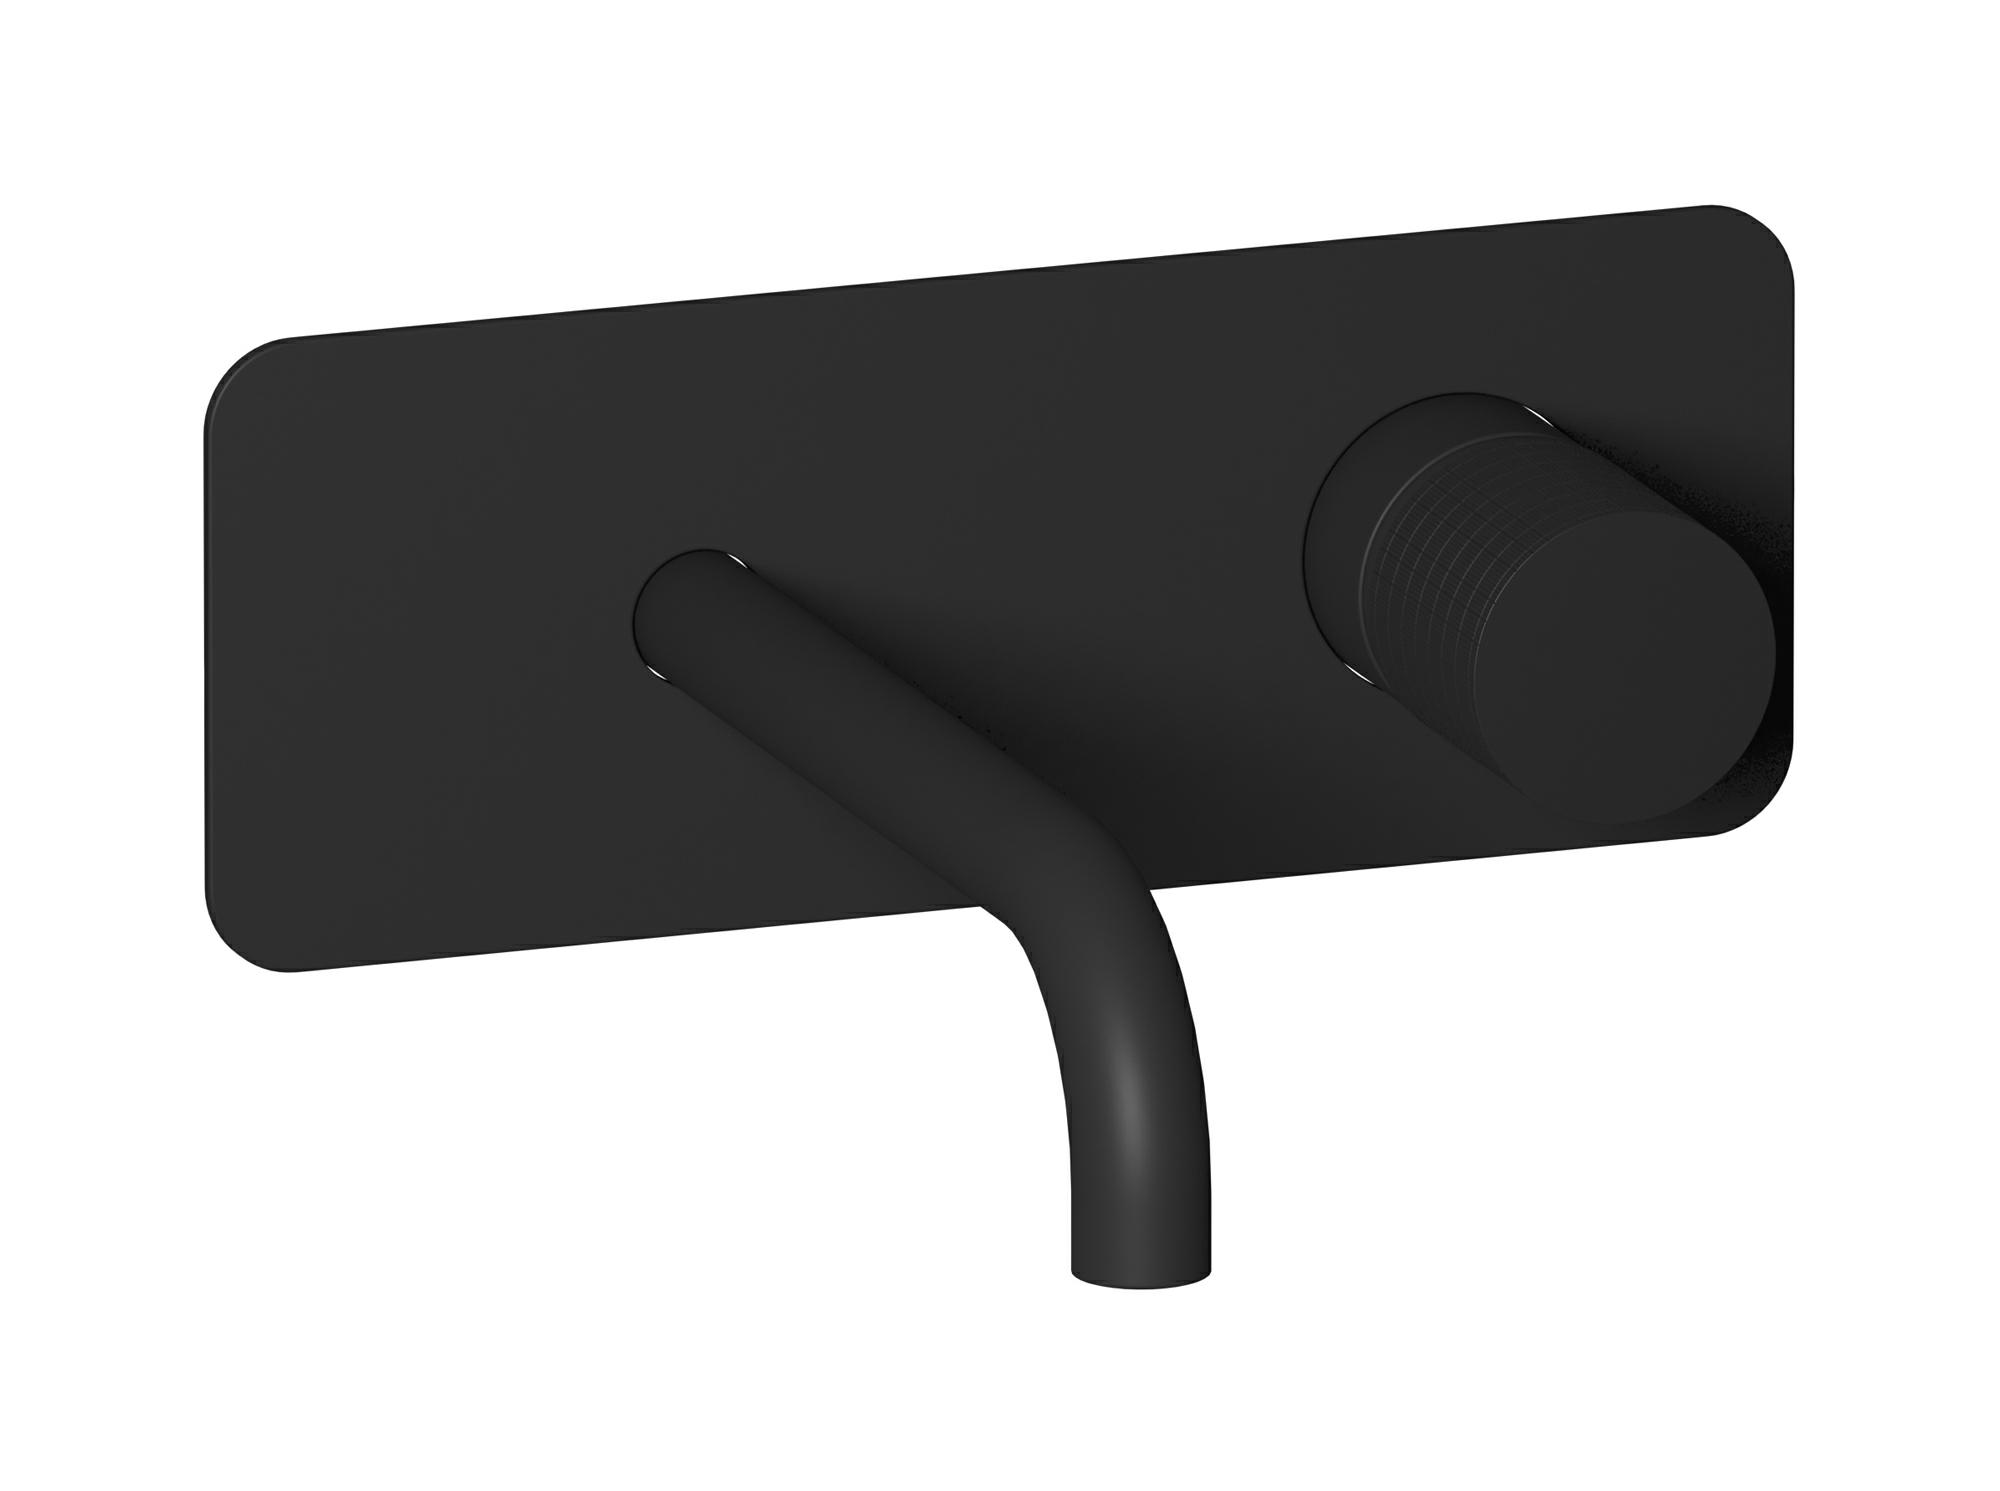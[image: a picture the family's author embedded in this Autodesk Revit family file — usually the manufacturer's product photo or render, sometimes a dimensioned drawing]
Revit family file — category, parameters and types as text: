
# Revit family: GA206
name_source: partatom
category: Apparecchi idraulici
units: mm (PartAtom-declared; Revit-internal decimal feet)

## family parameters
Basato su piano di lavoro = No
Condiviso = No
Mantieni orientamento annotazione = No
Numero OmniClass = 23.45.55.17
Punto di calcolo locali = No
Quota connettore circolare = Usa diametro
Sempre verticale = Sì
Taglio con vuoti quando caricato = No
Tipo di parte = Normale
Titolo OmniClass = Mixing Faucets

## types (12) — shared parameters
Cold water inlet = 10 mm  [stored 0.0328084 ft]
Commenti sul tipo = Wall mounted washbasin mixer complete with drain
Connessione CW = No
Connessione HW = No
Connessione di scarico = No
Connessione di ventilazione = No
Descrizione = Wall mounted washbasin mixer complete with drain
Hot water inlet = 10 mm  [stored 0.0328084 ft]
Produttore = IB Rubinetterie S.p.A.
URL = https://www.weareib.it
zero-valued in all types: Prospetto di default

## per-type parameters (varying)
| type | Finishes surface | Immagine tipo | Modello |
| Chrome | IB_Chrome | GA206CC.jpg | GA206CC |
| Brushed Nickel | IB_Brushed nickel | GA206SS.jpg | GA206SS |
| Matt Black | IB_matt black | GA206NP.jpg | GA206NP |
| Black Chrome | IB_Black chrome | GA206CF.jpg | GA206CF |
| Pale Gold | IB_Pale gold | GA206II.jpg | GA206II |
| Gold | IB_gold | GA206OO.jpg | GA206OO |
| Rose Gold | IB_Rose gold | GA206RS.jpg | GA206RS |
| Brushed Black Chrome | IB_Brushed black chrome | GA206CS.jpg | GA206CS |
| Brushed Pale Gold | IB_brushed pale gold | GA206IS.jpg | GA206IS |
| Brushed Gold | IB_brushed gold | GA206OS.jpg | GA206OS |
| Brushed Rose Gold | IB_Brushed rose gold | GA206SR.jpg | GA206SR |
| Modern Bronze | IB_Modern bronze | GA206MB.jpg | GA206MB |

note: [stored X ft] marks values corroborated as IEEE doubles in the binary element streams (Revit-internal decimal feet)
